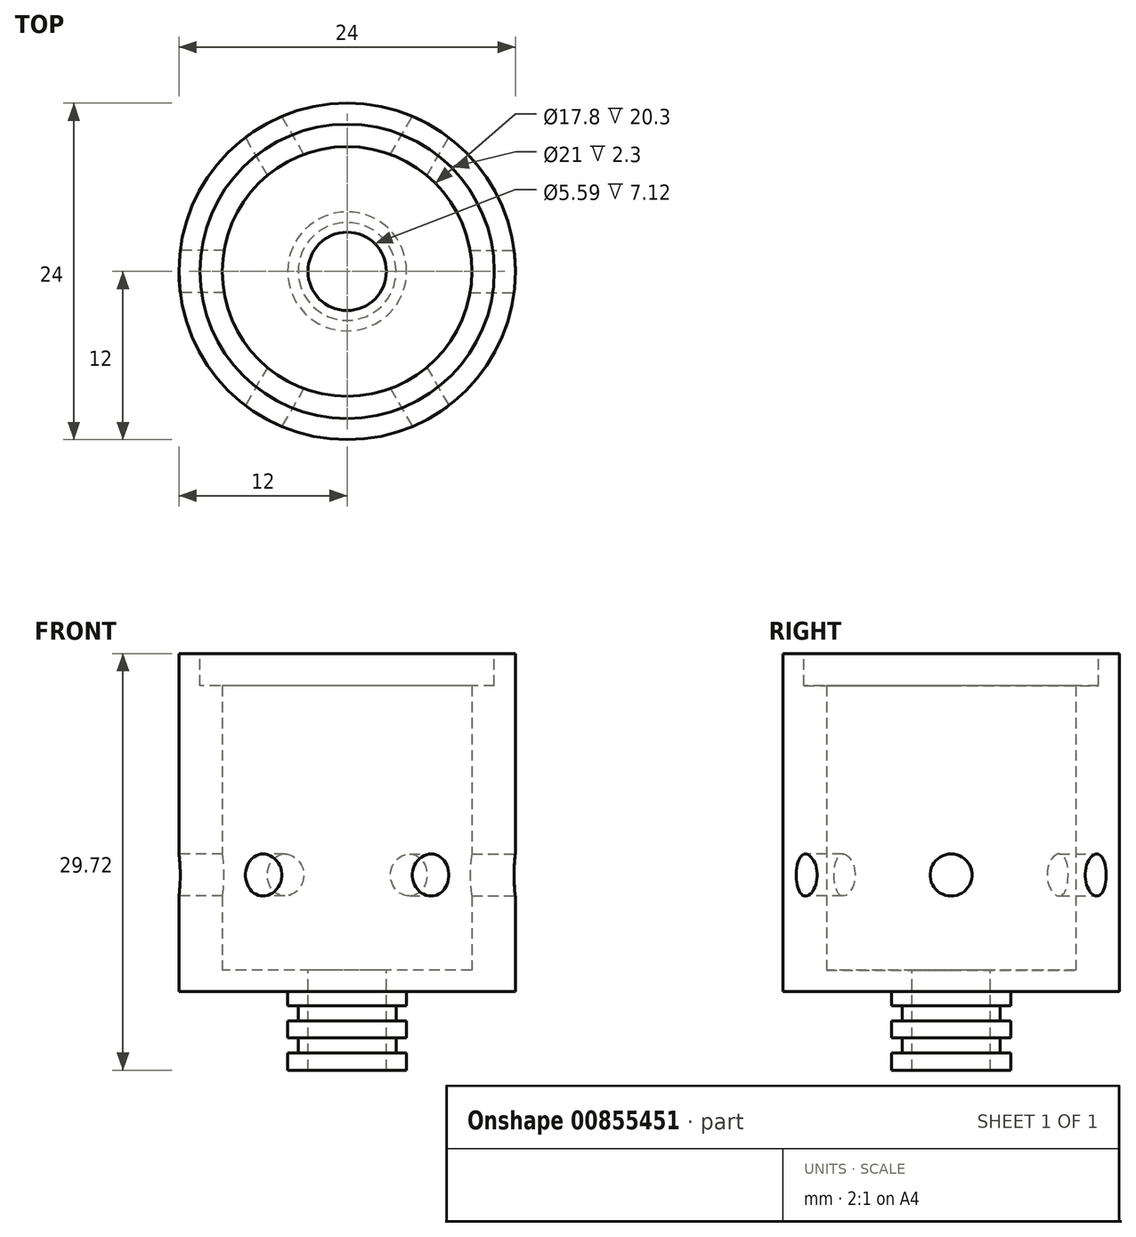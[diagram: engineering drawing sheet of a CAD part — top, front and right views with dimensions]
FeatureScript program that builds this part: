
annotation { "Feature Type Name" : "Feature", "Feature Type Description" : "" }
export const myFeature = defineFeature(function(context is Context, id is Id, definition is map)
    precondition{}
    {
        {
            var Q0;
            Q0=qCreatedBy(makeId("Top.planeOp"),FACE);
            var sketch = newSketch(context, id + "F0", { "sketchPlane" : qUnion([Q0])});
            skArc(sketch, "E0", {"start": v(7.7, -4.45) * mm, "mid": v(8.9, 0) * mm, "end": v(7.7, 4.45) * mm});
            skArc(sketch, "E1", {"start": v(10.4, -6) * mm, "mid": v(12, 0) * mm, "end": v(10.4, 6) * mm});
            skLineSegment(sketch, "E2", {"start": v(7.7, 4.45) * mm, "end": v(10.4, 6) * mm});
            skLineSegment(sketch, "E3.MirrorCS", {"start": v(7.7, -4.45) * mm, "end": v(10.4, -6) * mm});
            skSolve(sketch);
        }
        {
            var Q0;
            Q0=qSketchRegion(id+"F0",true);
            extrude(context, id + "F1", {"entities" : qUnion([Q0]), "depth" : 22.6 * mm, "offsetDistance" : 25 * mm});
        }
        {
            var Q0;
            Q0=qCreatedBy(makeId("Right.planeOp"),FACE);
            var sketch = newSketch(context, id + "F2", { "sketchPlane" : qUnion([Q0])});
            skCircle(sketch, "E4", {"center": v(0, 6.8) * mm, "radius": 1.5 * mm});
            skCircle(sketch, "E5", {"center": v(0, 11.3) * mm, "radius": 1.5 * mm, "construction": true});
            skCircle(sketch, "E6", {"center": v(0, 15.8) * mm, "radius": 1.5 * mm, "construction": true});
            skSolve(sketch);
        }
        {
            var Q0;
            Q0=qSketchRegion(id+"F2",true);
            extrude(context, id + "F3", {"entities" : qUnion([Q0]), "operationType" : NewBodyOperationType.REMOVE, "endBound" : BoundingType.THROUGH_ALL, "oppositeDirection" : true, "depth" : 25 * mm, "offsetDistance" : 25 * mm, "hasSecondDirection" : true, "secondDirectionBound" : SecondDirectionBoundingType.THROUGH_ALL, "secondDirectionOppositeDirection" : false, "secondDirectionDepth" : 25 * mm});
        }
        {
            var Q0;
            Q0=makeQuery(id+"F1.opExtrude","SWEPT_BODY",BODY,{"disambiguationData":[OSD([sQuery(id+"F0.wireOp",EDGE,"E0"),sQuery(id+"F0.wireOp",EDGE,"E1"),sQuery(id+"F0.wireOp",EDGE,"E2"),sQuery(id+"F0.wireOp",EDGE,"E3.MirrorCS")])]});
            var Q1;
            Q1=makeQuery(id+"F1.opExtrude","SWEPT_FACE",FACE,{"disambiguationData":[OSD([sQuery(id+"F0.wireOp",EDGE,"E1")])]});
            circularPattern(context, id + "F4", {"entities" : qUnion([Q0]), "axis" : qUnion([Q1]), "angle" : 360 * degree, "instanceCount" : 6, "equalSpace" : true});
        }
        {
            var Q0;
            Q0=makeQuery(id+"F1.opExtrude","SWEPT_BODY",BODY,{"disambiguationData":[OSD([sQuery(id+"F0.wireOp",EDGE,"E0"),sQuery(id+"F0.wireOp",EDGE,"E1"),sQuery(id+"F0.wireOp",EDGE,"E2"),sQuery(id+"F0.wireOp",EDGE,"E3.MirrorCS")])]});
            var Q1;
            Q1=makeQuery(id+"F4.opPattern","COPY",BODY,{"derivedFrom":makeQuery(id+"F1.opExtrude","SWEPT_BODY",BODY,{"disambiguationData":[OSD([sQuery(id+"F0.wireOp",EDGE,"E0"),sQuery(id+"F0.wireOp",EDGE,"E1"),sQuery(id+"F0.wireOp",EDGE,"E2"),sQuery(id+"F0.wireOp",EDGE,"E3.MirrorCS")])]}),"instanceName":"1"});
            var Q2;
            Q2=makeQuery(id+"F4.opPattern","COPY",BODY,{"derivedFrom":makeQuery(id+"F1.opExtrude","SWEPT_BODY",BODY,{"disambiguationData":[OSD([sQuery(id+"F0.wireOp",EDGE,"E0"),sQuery(id+"F0.wireOp",EDGE,"E1"),sQuery(id+"F0.wireOp",EDGE,"E2"),sQuery(id+"F0.wireOp",EDGE,"E3.MirrorCS")])]}),"instanceName":"2"});
            var Q3;
            Q3=makeQuery(id+"F4.opPattern","COPY",BODY,{"derivedFrom":makeQuery(id+"F1.opExtrude","SWEPT_BODY",BODY,{"disambiguationData":[OSD([sQuery(id+"F0.wireOp",EDGE,"E0"),sQuery(id+"F0.wireOp",EDGE,"E1"),sQuery(id+"F0.wireOp",EDGE,"E2"),sQuery(id+"F0.wireOp",EDGE,"E3.MirrorCS")])]}),"instanceName":"3"});
            var Q4;
            Q4=makeQuery(id+"F4.opPattern","COPY",BODY,{"derivedFrom":makeQuery(id+"F1.opExtrude","SWEPT_BODY",BODY,{"disambiguationData":[OSD([sQuery(id+"F0.wireOp",EDGE,"E0"),sQuery(id+"F0.wireOp",EDGE,"E1"),sQuery(id+"F0.wireOp",EDGE,"E2"),sQuery(id+"F0.wireOp",EDGE,"E3.MirrorCS")])]}),"instanceName":"4"});
            var Q5;
            Q5=makeQuery(id+"F4.opPattern","COPY",BODY,{"derivedFrom":makeQuery(id+"F1.opExtrude","SWEPT_BODY",BODY,{"disambiguationData":[OSD([sQuery(id+"F0.wireOp",EDGE,"E0"),sQuery(id+"F0.wireOp",EDGE,"E1"),sQuery(id+"F0.wireOp",EDGE,"E2"),sQuery(id+"F0.wireOp",EDGE,"E3.MirrorCS")])]}),"instanceName":"5"});
            booleanBodies(context, id + "F5", {"operationType" : BooleanOperationType.UNION, "tools" : qUnion([Q0, Q1, Q2, Q3, Q4, Q5])});
        }
        {
            var Q0;
            {var subQ0=makeQuery(id+"F1.opExtrude","CAP_FACE",FACE,{"disambiguationData":[OSD([sQuery(id+"F0.wireOp",EDGE,"E0"),sQuery(id+"F0.wireOp",EDGE,"E1"),sQuery(id+"F0.wireOp",EDGE,"E2"),sQuery(id+"F0.wireOp",EDGE,"E3.MirrorCS")])],"isStart":false});Q0=makeQuery(id+"F5.opBoolean","MERGE",FACE,{"derivedFrom":[subQ0,makeQuery(id+"F4.opPattern","COPY",FACE,{"derivedFrom":subQ0,"instanceName":"1"}),makeQuery(id+"F4.opPattern","COPY",FACE,{"derivedFrom":subQ0,"instanceName":"2"}),makeQuery(id+"F4.opPattern","COPY",FACE,{"derivedFrom":subQ0,"instanceName":"3"}),makeQuery(id+"F4.opPattern","COPY",FACE,{"derivedFrom":subQ0,"instanceName":"4"}),makeQuery(id+"F4.opPattern","COPY",FACE,{"derivedFrom":subQ0,"instanceName":"5"})]});}
            var sketch = newSketch(context, id + "F6", { "sketchPlane" : qUnion([Q0])});
            skCircle(sketch, "E7", {"center": v(0, 0) * mm, "radius": 10.5 * mm});
            skSolve(sketch);
        }
        {
            var Q0;
            Q0=qSketchRegion(id+"F6",true);
            extrude(context, id + "F7", {"entities" : qUnion([Q0]), "operationType" : NewBodyOperationType.REMOVE, "oppositeDirection" : true, "depth" : 2.3 * mm, "offsetDistance" : 25 * mm});
        }
        {
            var Q0;
            {var subQ0=makeQuery(id+"F1.opExtrude","CAP_FACE",FACE,{"disambiguationData":[OSD([sQuery(id+"F0.wireOp",EDGE,"E0"),sQuery(id+"F0.wireOp",EDGE,"E1"),sQuery(id+"F0.wireOp",EDGE,"E2"),sQuery(id+"F0.wireOp",EDGE,"E3.MirrorCS")])],"isStart":true});Q0=makeQuery(id+"F5.opBoolean","MERGE",FACE,{"derivedFrom":[subQ0,makeQuery(id+"F4.opPattern","COPY",FACE,{"derivedFrom":subQ0,"instanceName":"1"}),makeQuery(id+"F4.opPattern","COPY",FACE,{"derivedFrom":subQ0,"instanceName":"2"}),makeQuery(id+"F4.opPattern","COPY",FACE,{"derivedFrom":subQ0,"instanceName":"3"}),makeQuery(id+"F4.opPattern","COPY",FACE,{"derivedFrom":subQ0,"instanceName":"4"}),makeQuery(id+"F4.opPattern","COPY",FACE,{"derivedFrom":subQ0,"instanceName":"5"})]});}
            var sketch = newSketch(context, id + "F8", { "sketchPlane" : qUnion([Q0])});
            skCircle(sketch, "E8", {"center": v(0, 0) * mm, "radius": 10.5 * mm});
            skSolve(sketch);
        }
        {
            var Q0;
            Q0=qSketchRegion(id+"F8",true);
            extrude(context, id + "F9", {"entities" : qUnion([Q0]), "operationType" : NewBodyOperationType.REMOVE, "oppositeDirection" : true, "depth" : 2.3 * mm, "offsetDistance" : 25 * mm});
        }
        {
            var Q0;
            Q0=qCreatedBy(makeId("Front.planeOp"),FACE);
            var sketch = newSketch(context, id + "F10", { "sketchPlane" : qUnion([Q0])});
            skLineSegment(sketch, "E9", {"start": v(10.5, 0) * mm, "end": v(10.5, 2.3) * mm});
            skLineSegment(sketch, "E10", {"start": v(-10.5, 2.3) * mm, "end": v(-10.5, 0) * mm});
            skLineSegment(sketch, "E11", {"start": v(-10.5, 0) * mm, "end": v(-12, 0) * mm});
            skLineSegment(sketch, "E12", {"start": v(12, 0) * mm, "end": v(10.5, 0) * mm});
            skLineSegment(sketch, "E13", {"start": v(8.9, 2.3) * mm, "end": v(10.5, 2.3) * mm});
            skLineSegment(sketch, "E14", {"start": v(-10.5, 2.3) * mm, "end": v(-8.9, 2.3) * mm});
            skLineSegment(sketch, "E15", {"start": v(12, 0) * mm, "end": v(12, -1.5) * mm});
            skLineSegment(sketch, "E16", {"start": v(12, -1.5) * mm, "end": v(4.25, -1.5) * mm});
            skLineSegment(sketch, "E17", {"start": v(4.25, -1.5) * mm, "end": v(4.25, -2.53) * mm});
            skLineSegment(sketch, "E18", {"start": v(4.25, -7.12) * mm, "end": v(2.8, -7.12) * mm});
            skLineSegment(sketch, "E19", {"start": v(2.8, -7.12) * mm, "end": v(2.8, 0) * mm});
            skLineSegment(sketch, "E20", {"start": v(2.8, 0) * mm, "end": v(8.9, 0) * mm});
            skLineSegment(sketch, "E21", {"start": v(8.9, 0) * mm, "end": v(8.9, 2.3) * mm});
            skLineSegment(sketch, "E22", {"start": v(0, 0) * mm, "end": v(0, -12.01) * mm, "construction": true});
            skLineSegment(sketch, "E23", {"start": v(3.5, -4.8) * mm, "end": v(3.5, -5.89) * mm});
            skLineSegment(sketch, "E24", {"start": v(3.5, -5.89) * mm, "end": v(4.25, -5.89) * mm});
            skLineSegment(sketch, "E25", {"start": v(3.5, -4.8) * mm, "end": v(4.25, -4.8) * mm});
            skLineSegment(sketch, "E26", {"start": v(4.25, -3.6) * mm, "end": v(3.5, -3.6) * mm});
            skLineSegment(sketch, "E27", {"start": v(3.5, -3.6) * mm, "end": v(3.5, -2.53) * mm});
            skLineSegment(sketch, "E28", {"start": v(3.5, -2.53) * mm, "end": v(4.25, -2.53) * mm});
            skLineSegment(sketch, "E29.trimOffspring", {"start": v(4.25, -3.6) * mm, "end": v(4.25, -4.8) * mm});
            skLineSegment(sketch, "E30.trimOffspring", {"start": v(4.25, -5.89) * mm, "end": v(4.25, -7.12) * mm});
            skSolve(sketch);
        }
        {
            var Q0;
            Q0=qSketchRegion(id+"F10",true);
            var Q1;
            Q1=sQuery(id+"F10.wireOp",EDGE,"E22");
            revolve(context, id + "F11", {"operationType" : NewBodyOperationType.ADD, "surfaceOperationType" : NewSurfaceOperationType.NEW, "entities" : qUnion([Q0]), "axis" : qUnion([Q1]), "revolveType" : RevolveType.FULL});
        }
    });
